# Revit family: Combination_Seat_Cover_Tissue_Dispenser_Napkin_Disposal-Bobrick-ClassicSeries-B-35745
name_source: partatom
category: Specialty Equipment
revit_build: Autodesk Revit 2014 (Build: 20130308_1515(x64)
units: mm (PartAtom-declared; Revit-internal decimal feet)

## types (1)
- B-35745
    Assembly Code = E1090900
    Default Elevation = 38 23/32"
    Description = ClassicSeries® Recessed Seat-Cover Dispenser, Sanitary Napkin Disposal, and Toilet Tissue Dispenser
    Finish = Stainless Steel-Bobrick-Type 304-Satin
    Height = 30 5/8"
    Installation Type = Wall Mounted
    Length = 3 15/16"
    Manufacturer = Bobrick
    Material = Stainless Steel-Bobrick-Type 304-Satin
    Model = B-35745
    Price = Prices may vary. Please consult Manufacturer Representative for most up-to-date price list.
    Product Documentation Link = http://www.bobrick.com
    Product Page URL = http://www.bobrick.com
    Revised Date = 04/11/2018
    URL = http://www.bobrick.com
    Warranty Information = 1 Year Limited Warranty
    Width = 17 3/16"

## geometry (parser evidence)
native form markers: Sweep x3
no freeform markers — native parametric forms only
